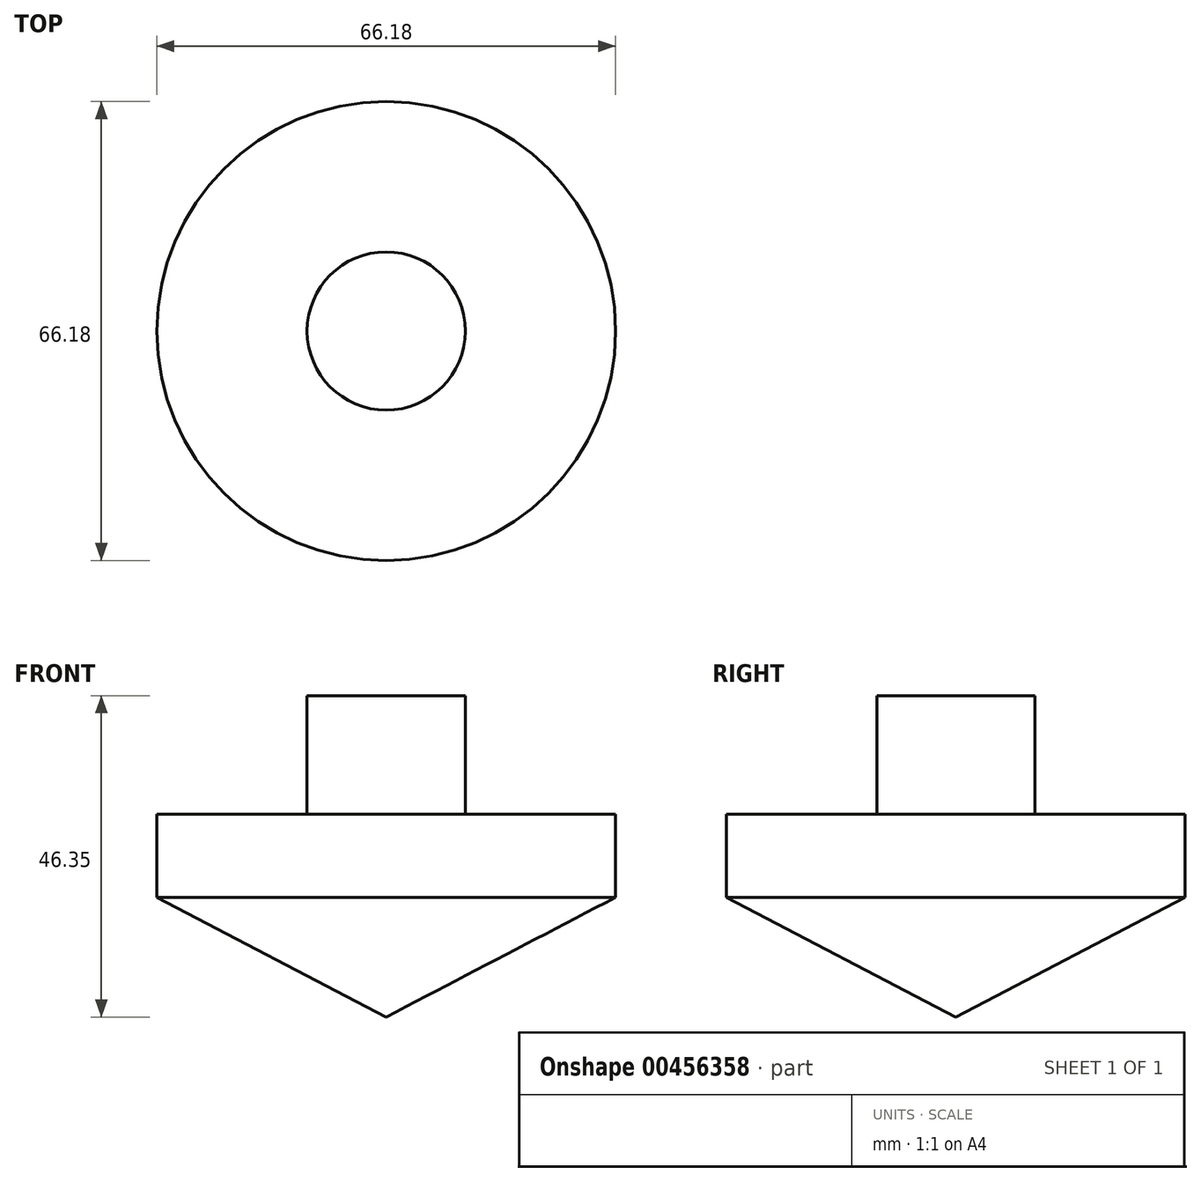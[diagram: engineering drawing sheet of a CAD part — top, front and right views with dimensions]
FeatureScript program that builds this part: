
annotation { "Feature Type Name" : "Feature", "Feature Type Description" : "" }
export const myFeature = defineFeature(function(context is Context, id is Id, definition is map)
    precondition{}
    {
        {
            var Q0;
            Q0=qCreatedBy(makeId("Front.planeOp"),FACE);
            var sketch = newSketch(context, id + "F0", { "sketchPlane" : qUnion([Q0])});
            skLineSegment(sketch, "E0", {"start": v(0, 0) * mm, "end": v(33.09, 17.26) * mm});
            skLineSegment(sketch, "E1", {"start": v(33.09, 17.26) * mm, "end": v(33.09, 29.24) * mm});
            skLineSegment(sketch, "E2", {"start": v(33.09, 29.24) * mm, "end": v(11.4, 29.24) * mm});
            skLineSegment(sketch, "E3", {"start": v(11.4, 29.24) * mm, "end": v(11.4, 46.35) * mm});
            skLineSegment(sketch, "E4", {"start": v(11.4, 46.35) * mm, "end": v(0, 46.35) * mm});
            skLineSegment(sketch, "E5", {"start": v(0, 46.35) * mm, "end": v(0, 0) * mm});
            skSolve(sketch);
        }
        {
            var Q0;
            Q0=makeQuery(id+"F0.imprint","IMPRINT",FACE,{"disambiguationData":[TD([[makeQuery(id+"F0.imprint","IMPRINT",EDGE,{"derivedFrom":sQuery(id+"F0.wireOp",EDGE,"E0")}),1.0]])]});
            var Q1;
            Q1=sQuery(id+"F0.wireOp",EDGE,"E5");
            revolve(context, id + "F1", {"entities" : qUnion([Q0]), "axis" : qUnion([Q1]), "revolveType" : RevolveType.FULL});
        }
    });
